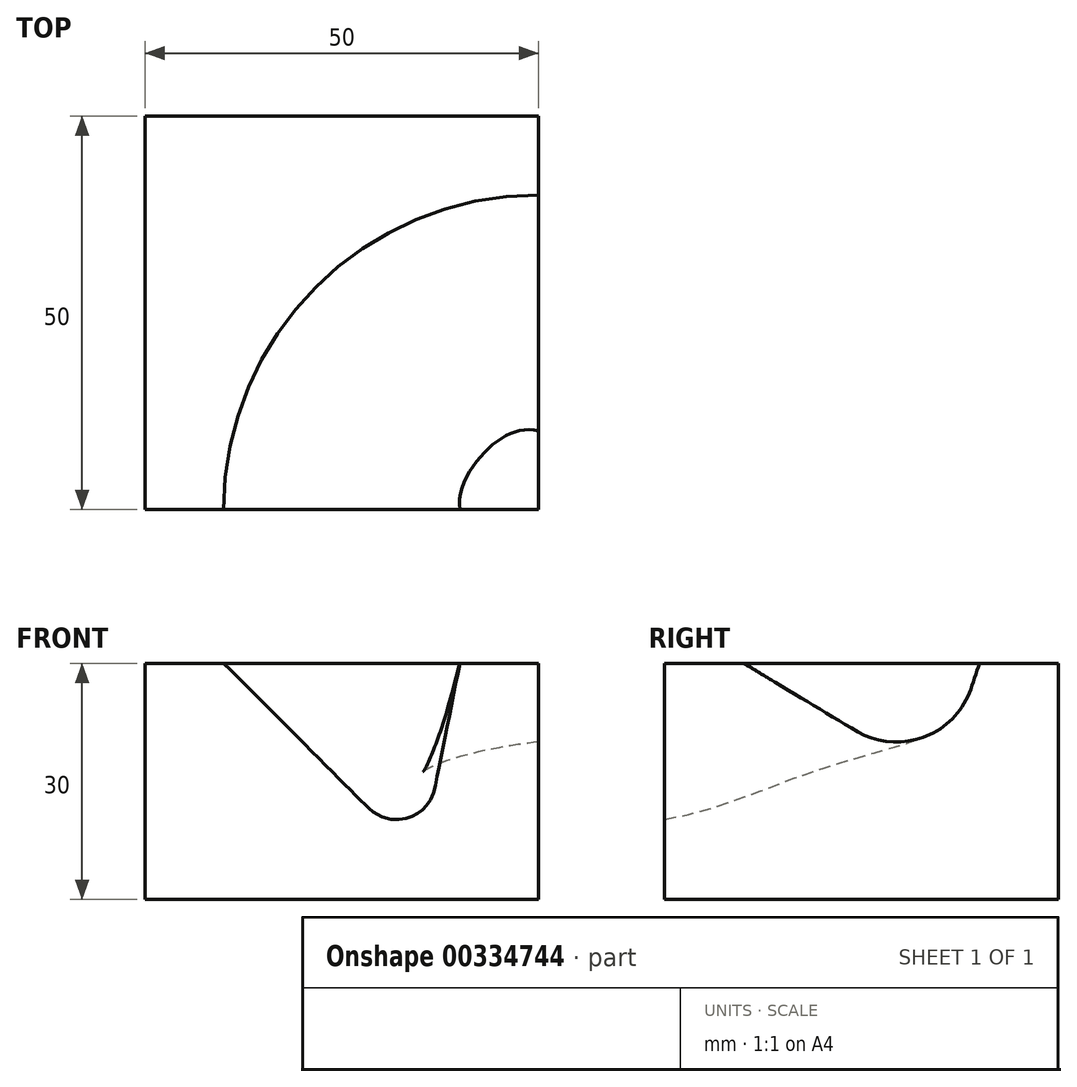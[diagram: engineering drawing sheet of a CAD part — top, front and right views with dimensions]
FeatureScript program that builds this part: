
annotation { "Feature Type Name" : "Feature", "Feature Type Description" : "" }
export const myFeature = defineFeature(function(context is Context, id is Id, definition is map)
    precondition{}
    {
        {
            var Q0;
            Q0=qCreatedBy(makeId("Top.planeOp"),FACE);
            var sketch = newSketch(context, id + "F0", { "sketchPlane" : qUnion([Q0])});
            skLineSegment(sketch, "E0.bottom", {"start": v(-25, 25) * mm, "end": v(25, 25) * mm});
            skLineSegment(sketch, "E0.top", {"start": v(-25, -25) * mm, "end": v(25, -25) * mm});
            skLineSegment(sketch, "E0.left", {"start": v(-25, 25) * mm, "end": v(-25, -25) * mm});
            skLineSegment(sketch, "E0.right", {"start": v(25, 25) * mm, "end": v(25, -25) * mm});
            skPoint(sketch, "E0.middle", {"position": v(0, 0) * mm});
            skSolve(sketch);
        }
        {
            var Q0;
            Q0=makeQuery(id+"F0.imprint","IMPRINT",FACE,{"disambiguationData":[TD([[makeQuery(id+"F0.imprint","IMPRINT",EDGE,{"derivedFrom":sQuery(id+"F0.wireOp",EDGE,"E0.bottom")}),-1.0]])]});
            extrude(context, id + "F1", {"entities" : qUnion([Q0]), "depth" : 30 * mm});
        }
        {
            var Q0;
            Q0=makeQuery(id+"F1.opExtrude","SWEPT_FACE",FACE,{"disambiguationData":[OSD([sQuery(id+"F0.wireOp",EDGE,"E0.right")])]});
            var sketch = newSketch(context, id + "F2", { "sketchPlane" : qUnion([Q0])});
            skLineSegment(sketch, "E1", {"start": v(-15, 30) * mm, "end": v(-0.69, 21.41) * mm});
            skLineSegment(sketch, "E2", {"start": v(13.94, 26.83) * mm, "end": v(15, 30) * mm});
            skPoint(sketch, "E3.visualSharp", {"position": v(10, 15) * mm});
            skArc(sketch, "E3.filletArc", {"start": v(-0.69, 21.41) * mm, "mid": v(7.92, 20.6) * mm, "end": v(13.94, 26.83) * mm});
            skSolve(sketch);
        }
        {
            var Q0;
            Q0=makeQuery(id+"F1.opExtrude","SWEPT_FACE",FACE,{"disambiguationData":[OSD([sQuery(id+"F0.wireOp",EDGE,"E0.top")])]});
            var sketch = newSketch(context, id + "F3", { "sketchPlane" : qUnion([Q0])});
            skLineSegment(sketch, "E4", {"start": v(-15, 30) * mm, "end": v(3.4, 11.6) * mm});
            skLineSegment(sketch, "E5", {"start": v(11.83, 14.16) * mm, "end": v(15, 30) * mm});
            skPoint(sketch, "E6.visualSharp", {"position": v(10, 5) * mm});
            skArc(sketch, "E6.filletArc", {"start": v(3.4, 11.6) * mm, "mid": v(8.38, 10.36) * mm, "end": v(11.83, 14.16) * mm});
            skSolve(sketch);
        }
        {
            var Q0;
            Q0=makeQuery(id+"F1.opExtrude","CAP_FACE",FACE,{"disambiguationData":[OSD([sQuery(id+"F0.wireOp",EDGE,"E0.bottom"),sQuery(id+"F0.wireOp",EDGE,"E0.top"),sQuery(id+"F0.wireOp",EDGE,"E0.left"),sQuery(id+"F0.wireOp",EDGE,"E0.right")])],"isStart":false});
            var sketch = newSketch(context, id + "F4", { "sketchPlane" : qUnion([Q0])});
            skCircle(sketch, "E7", {"center": v(25, -25) * mm, "radius": 10 * mm});
            skCircle(sketch, "E8", {"center": v(25, -25) * mm, "radius": 40 * mm});
            skSolve(sketch);
        }
        {
            var Q1;
            {var subQ0=sQuery(id+"F3.wireOp",EDGE,"E4");Q1=makeQuery(id+"F3.imprint","IMPRINT",FACE,{"disambiguationData":[TD([[makeQuery(id+"F3.imprint","IMPRINT",EDGE,{"derivedFrom":subQ0}),1.0]])]});}
            var Q2;
            {var subQ0=sQuery(id+"F2.wireOp",EDGE,"E1");Q2=makeQuery(id+"F2.imprint","IMPRINT",FACE,{"disambiguationData":[TD([[makeQuery(id+"F2.imprint","IMPRINT",EDGE,{"derivedFrom":subQ0}),1.0]])]});}
            var Q3;
            Q3=sQuery(id+"F4.wireOp",EDGE,"E8");
            loft(context, id + "F5", {"operationType" : NewBodyOperationType.REMOVE, "addGuides" : true, "sheetProfilesArray" : [{ "sheetProfileEntities" : qUnion([Q1]) }, { "sheetProfileEntities" : qUnion([Q2]) }], "guidesArray" : [{ "guideEntities" : qUnion([Q3]), "guideDerivativeType" : LoftGuideDerivativeType.DEFAULT, "guideDerivativeMagnitude" : 1 }]});
        }
    });
